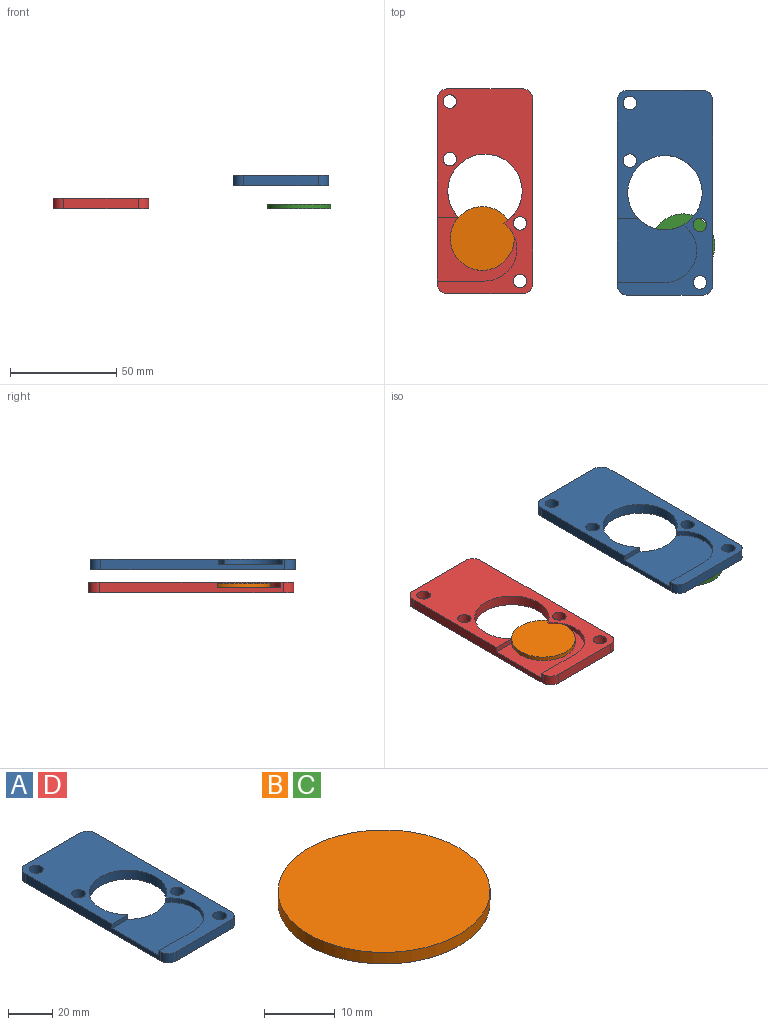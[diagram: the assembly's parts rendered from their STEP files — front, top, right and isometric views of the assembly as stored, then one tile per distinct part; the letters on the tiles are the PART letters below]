
ASSEMBLY  parts=4 mates=1
PART A: 19 faces, bbox 45x96.5x5 mm
  f0: plane 96.5x45mm, normal (0,0,1), area 2280.5mm2, adj f2,f3,f4,f5,f6,f7,f8,f10
  f1: plane 96.5x45mm, normal (0,0,-1), area 3232.3mm2, adj f4,f5,f6,f7,f10,f11,f12,f13
  f2: plane 10x2.5mm, normal (0,-1,0), area 25mm2, adj f0,f4,f9,f10
  f3: cylinder r=15mm len=27.13mm, axis (0,0,1), area 94.2mm2, adj f0,f8,f9,f10
  f4: plane 86.5x5mm, normal (-1,0,0), area 357.5mm2, adj f0,f1,f2,f8,f9,f12,f13
  f5: plane 86.5x5mm, normal (1,0,0), area 432.5mm2, adj f0,f1,f11,f14
  f6: plane 35x5mm, normal (0,1,0), area 175mm2, adj f0,f1,f11,f12
  f7: plane 35x5mm, normal (0,-1,0), area 175mm2, adj f0,f1,f13,f14
  f8: plane 22.5x2.5mm, normal (0,1,0), area 56.3mm2, adj f0,f3,f4,f9
  f9: plane 37.5x30mm, normal (0,0,1), area 951.8mm2, adj f2,f3,f4,f8,f10
  f10: cylinder r=17.5mm len=35mm, axis (0,0,-1), area 491.9mm2, adj f0,f1,f2,f3,f9
  f11: cylinder r=5mm len=5mm, axis (0,0,-1), area 39.3mm2, adj f0,f1,f5,f6
  f12: cylinder r=5mm len=5mm, axis (0,0,1), area 39.3mm2, adj f0,f1,f4,f6
  f13: cylinder r=5mm len=5mm, axis (0,0,-1), area 39.3mm2, adj f0,f1,f4,f7
  f14: cylinder r=5mm len=5mm, axis (0,0,1), area 39.3mm2, adj f0,f1,f5,f7
  f15: cylinder r=3.17mm len=6.35mm, axis (0,0,-1), area 99.7mm2, adj f0,f1
  f16: cylinder r=3.17mm len=6.35mm, axis (0,0,-1), area 99.7mm2, adj f0,f1
  f17: cylinder r=3.17mm len=6.35mm, axis (0,0,-1), area 99.7mm2, adj f0,f1
  f18: cylinder r=3.17mm len=6.35mm, axis (0,0,-1), area 99.7mm2, adj f0,f1
PART B: 3 faces, bbox 30x30x2 mm
  f0: cylinder r=15mm len=30mm, axis (0,0,-1), area 188.5mm2, adj f1,f2
  f1: plane 30x30mm, normal (0,0,1), area 706.9mm2, adj f0
  f2: plane 30x30mm, normal (0,0,-1), area 706.9mm2, adj f0
PART C: same geometry as B
PART D: same geometry as A
PLACE A t=(75.24,0,0)mm
PLACE B rot(axis=(1,0,0),180deg) t=(-10.73,-21.54,-11.31)mm
PLACE C t=(83.73,-24.95,-15.77)mm
PLACE D t=(-9.47,0.71,-10.81)mm
MATE planar B.f0 <-> D.f9  axis (0,0,-1) through (-10.73,-21.54,-13.31)mm
